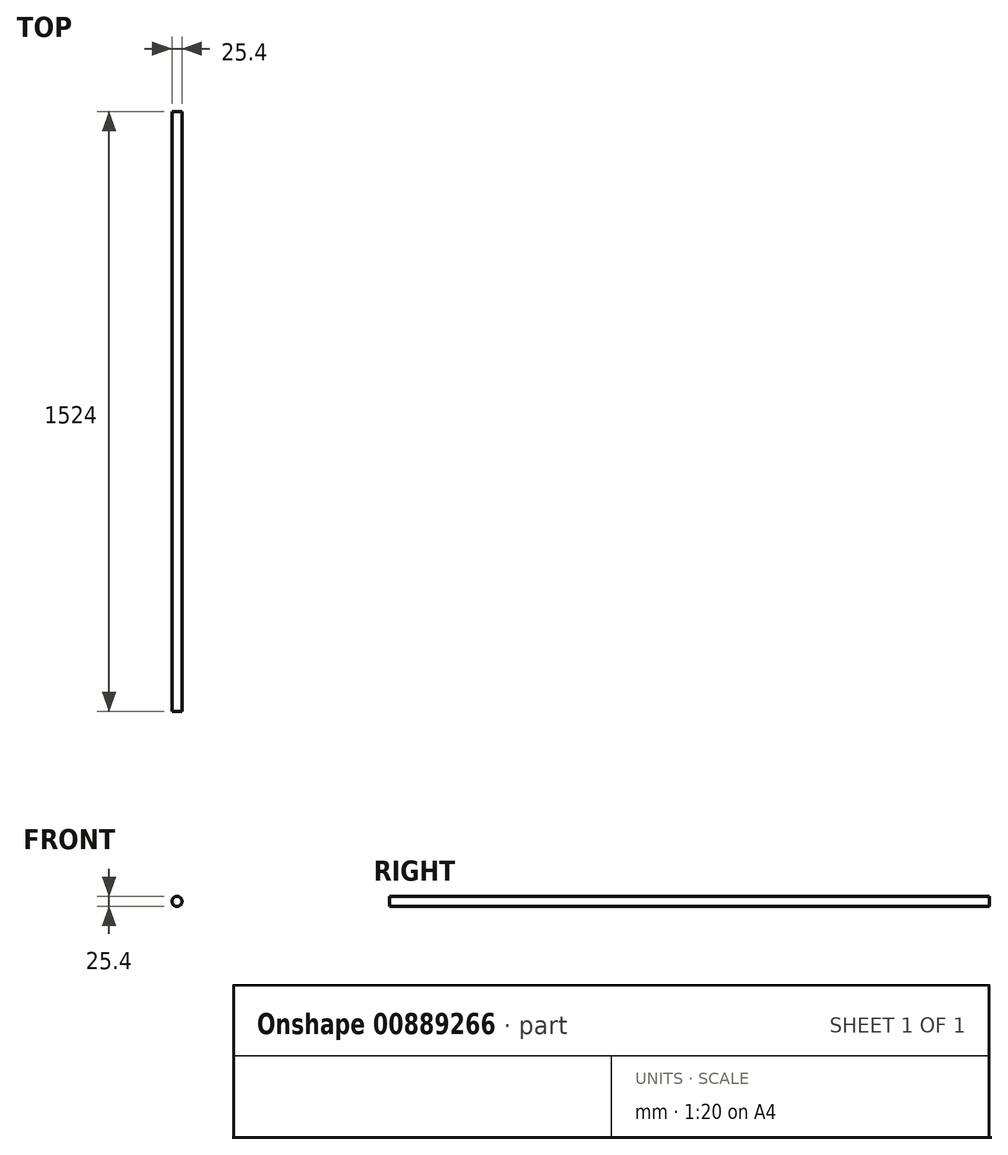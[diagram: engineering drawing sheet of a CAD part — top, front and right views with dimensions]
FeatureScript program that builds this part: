
annotation { "Feature Type Name" : "Feature", "Feature Type Description" : "" }
export const myFeature = defineFeature(function(context is Context, id is Id, definition is map)
    precondition{}
    {
        {
            var Q0;
            Q0=qCreatedBy(makeId("Front.planeOp"),FACE);
            var sketch = newSketch(context, id + "F0", { "sketchPlane" : qUnion([Q0])});
            skCircle(sketch, "E0", {"center": v(0, 0) * mm, "radius": 12.7 * mm});
            skSolve(sketch);
        }
        {
            var Q0;
            Q0 = qSketchRegion(id + "F0", true);
            extrude(context, id + "F1", {"entities" : qUnion([Q0]), "depth" : 1524 * mm, "offsetDistance" : 25.4 * mm});
        }
    });
